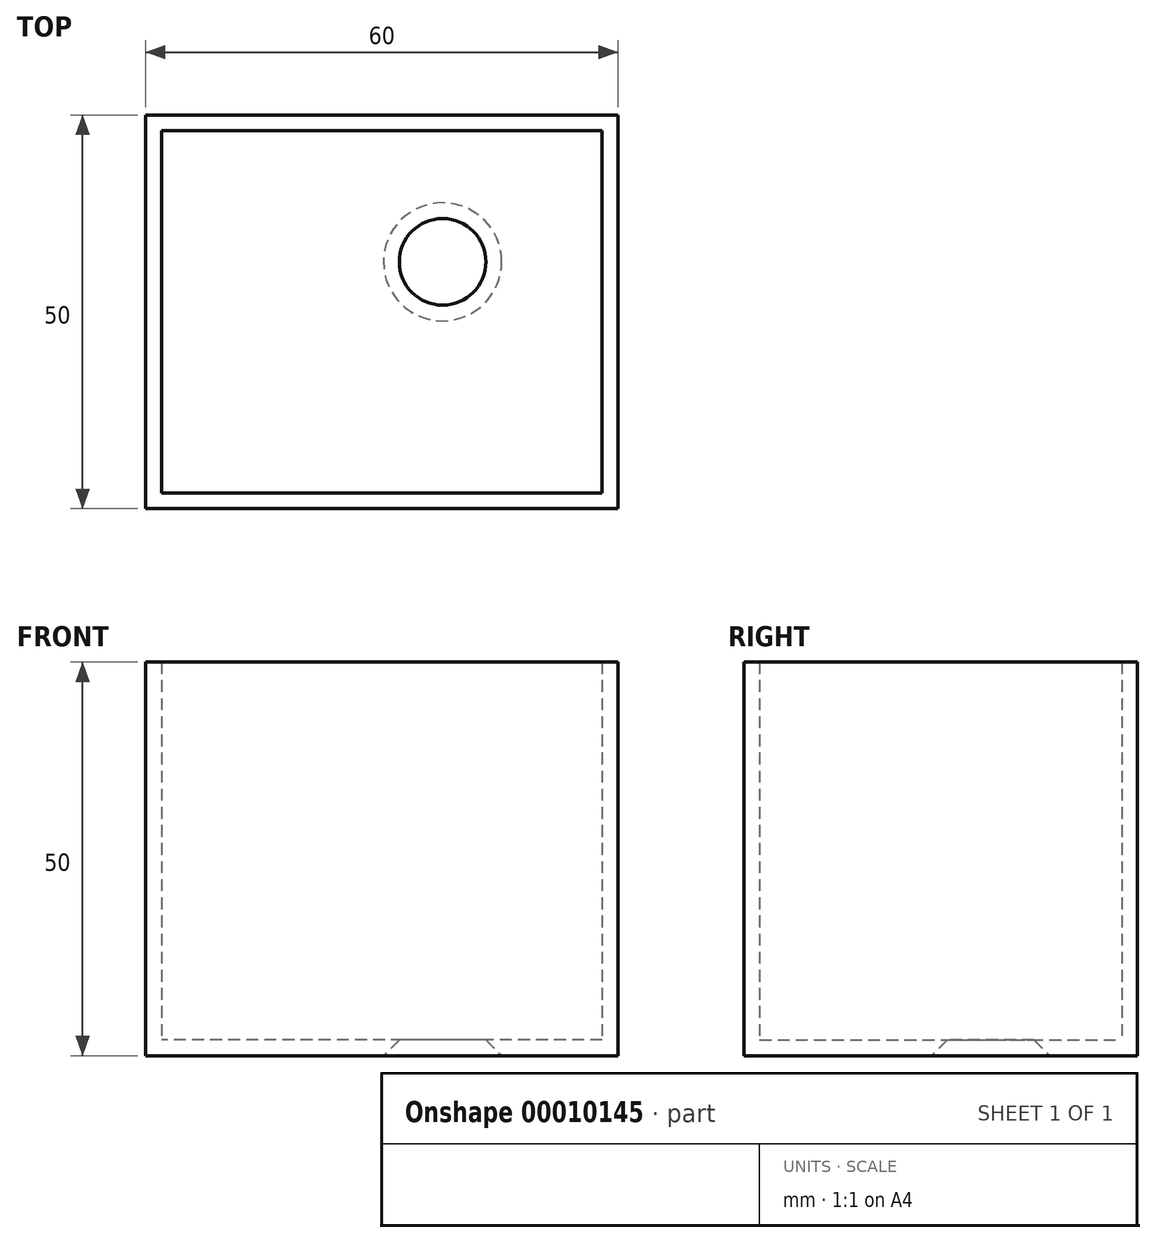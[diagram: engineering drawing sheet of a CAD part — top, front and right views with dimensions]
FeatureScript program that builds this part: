
annotation { "Feature Type Name" : "Feature", "Feature Type Description" : "" }
export const myFeature = defineFeature(function(context is Context, id is Id, definition is map)
    precondition{}
    {
        {
            var Q0;
            Q0=qCreatedBy(makeId("Top.planeOp"),FACE);
            var sketch = newSketch(context, id + "F0", { "sketchPlane" : qUnion([Q0])});
            skLineSegment(sketch, "E0.rect.bottom", {"start": v(30, -25) * mm, "end": v(-30, -25) * mm});
            skLineSegment(sketch, "E0.rect.top", {"start": v(30, 25) * mm, "end": v(-30, 25) * mm});
            skLineSegment(sketch, "E0.rect.left", {"start": v(30, -25) * mm, "end": v(30, 25) * mm});
            skLineSegment(sketch, "E0.rect.right", {"start": v(-30, -25) * mm, "end": v(-30, 25) * mm});
            skPoint(sketch, "E0.rect.middle", {"position": v(0, 0) * mm});
            skSolve(sketch);
        }
        {
            var Q0;
            Q0=makeQuery(id+"F0.imprint","IMPRINT",FACE,{"disambiguationData":[TD([[makeQuery(id+"F0.imprint","IMPRINT",EDGE,{"derivedFrom":sQuery(id+"F0.wireOp",EDGE,"E0.rect.bottom")}),-1.0]])]});
            extrude(context, id + "F1", {"entities" : qUnion([Q0]), "depth" : 50 * mm});
        }
        {
            var Q0;
            Q0=makeQuery(id+"F1.opExtrude","CAP_FACE",FACE,{"disambiguationData":[OSD([sQuery(id+"F0.wireOp",EDGE,"E0.rect.bottom"),sQuery(id+"F0.wireOp",EDGE,"E0.rect.top"),sQuery(id+"F0.wireOp",EDGE,"E0.rect.left"),sQuery(id+"F0.wireOp",EDGE,"E0.rect.right")])],"isStart":false});
            shell(context, id + "F2", {"entities" : qUnion([Q0]), "thickness" : 2 * mm});
        }
        {
            var Q0;
            Q0=makeQuery(id+"F2.opShell","OFFSET_FACE",FACE,{"disambiguationData":[OSD([sQuery(id+"F0.wireOp",EDGE,"E0.rect.bottom"),sQuery(id+"F0.wireOp",EDGE,"E0.rect.top"),sQuery(id+"F0.wireOp",EDGE,"E0.rect.left"),sQuery(id+"F0.wireOp",EDGE,"E0.rect.right")])]});
            var sketch = newSketch(context, id + "F3", { "sketchPlane" : qUnion([Q0])});
            skLineSegment(sketch, "E1", {"start": v(0, 0) * mm, "end": v(28, 23) * mm});
            skCircle(sketch, "E2", {"center": v(7.73, 6.35) * mm, "radius": 2.5 * mm});
            skLineSegment(sketch, "E3", {"start": v(7.73, 6.35) * mm, "end": v(0, 0) * mm});
            skCircle(sketch, "E4", {"center": v(-4.73, -8.81) * mm, "radius": 2.5 * mm});
            skLineSegment(sketch, "E5", {"start": v(-28, 23) * mm, "end": v(28, -23) * mm});
            skLineSegment(sketch, "E6", {"start": v(-28, -23) * mm, "end": v(0, 0) * mm});
            skLineSegment(sketch, "E7", {"start": v(7.73, 6.35) * mm, "end": v(1.5, -1.23) * mm});
            skLineSegment(sketch, "E8", {"start": v(-4.73, -8.81) * mm, "end": v(1.5, -1.23) * mm});
            skSolve(sketch);
        }
        {
            var Q0;
            {var subQ1=sQuery(id+"F3.wireOp",EDGE,"E2");var subQ3=sQuery(id+"F3.wireOp",EDGE,"E1");var subQ5=makeQuery(id+"F3.imprint","INTERSECT",VERTEX,{"derivedFrom":[subQ3,subQ1]});Q0=makeQuery(id+"F3.imprint","IMPRINT",FACE,{"disambiguationData":[TD([[makeQuery(id+"F3.imprint","IMPRINT",EDGE,{"disambiguationData":[TD([[subQ5,1.0]])],"derivedFrom":subQ1}),1.0]])]});}
            var Q1;
            {var subQ1=sQuery(id+"F3.wireOp",EDGE,"E2");var subQ3=sQuery(id+"F3.wireOp",EDGE,"E1");var subQ5=makeQuery(id+"F3.imprint","INTERSECT",VERTEX,{"derivedFrom":[subQ3,subQ1]});Q1=makeQuery(id+"F3.imprint","IMPRINT",FACE,{"disambiguationData":[TD([[makeQuery(id+"F3.imprint","IMPRINT",EDGE,{"disambiguationData":[TD([[subQ5,-1.0]])],"derivedFrom":subQ1}),1.0]])]});}
            var Q2;
            {var subQ1=sQuery(id+"F3.wireOp",EDGE,"E2");var subQ3=sQuery(id+"F3.wireOp",EDGE,"E3");var subQ5=makeQuery(id+"F3.imprint","INTERSECT",VERTEX,{"derivedFrom":[subQ1,subQ3]});Q2=makeQuery(id+"F3.imprint","IMPRINT",FACE,{"disambiguationData":[TD([[makeQuery(id+"F3.imprint","IMPRINT",EDGE,{"disambiguationData":[TD([[subQ5,-1.0]])],"derivedFrom":subQ1}),1.0]])]});}
            extrude(context, id + "F4", {"entities" : qUnion([Q0, Q1, Q2]), "operationType" : NewBodyOperationType.REMOVE, "oppositeDirection" : true, "depth" : 25 * mm});
        }
        {
            var Q0;
            Q0=makeQuery(id+"F4.boolean.opBoolean","INTERSECT",EDGE,{"derivedFrom":[makeQuery(id+"F1.opExtrude","CAP_FACE",FACE,{"disambiguationData":[OSD([sQuery(id+"F0.wireOp",EDGE,"E0.rect.bottom"),sQuery(id+"F0.wireOp",EDGE,"E0.rect.top"),sQuery(id+"F0.wireOp",EDGE,"E0.rect.left"),sQuery(id+"F0.wireOp",EDGE,"E0.rect.right")])],"isStart":true}),makeQuery(id+"F4.opExtrude","SWEPT_FACE",FACE,{"disambiguationData":[OSD([sQuery(id+"F3.wireOp",EDGE,"E2")])]})]});
            chamfer(context, id + "F5", {"entities" : qUnion([Q0]), "width" : 5 * mm, "tangentPropagation" : true});
        }
    });
